FCSTD DOCUMENT  (FreeCAD 0.20R29603 (Git))
Label: assy
License: All rights reserved
LicenseURL: http://en.wikipedia.org/wiki/All_rights_reserved
objects: App::DocumentObjectGroup×3, App::Link×2, PartDesign::CoordinateSystem×1, App::FeaturePython×1, App::Part×1
note: 1 computed .brp shape members not serialized (recipe doc carries the construction recipe); baked Part::Feature solids carry a one-line shape summary decoded from their .brp
EXTERNAL_REF file=spindle.FCStd obj=LCS_1
EXTERNAL_REF file=spindle.FCStd obj=Body
EXTERNAL_REF file=nozzle.FCStd obj=LCS_1
EXTERNAL_REF file=nozzle.FCStd obj=Body

FEATURE [App::DocumentObjectGroup] Parts
FEATURE [PartDesign::CoordinateSystem] LCS_Origin
  AttacherType = Attacher::AttachEngine3D
  MapMode = 2
  Support = -> [X_Axis]
FEATURE [App::DocumentObjectGroup] Constraints
FEATURE [App::FeaturePython] Variables  # WARN: FeaturePython — macro-defined, semantics opaque (R4)
  Type = App::PropertyContainer
FEATURE [App::DocumentObjectGroup] Configurations
FEATURE [App::Link] Body
  AssemblyType = Part::Link
  AttachedBy = #LCS_1
  AttachedTo = Parent Assembly#LCS_Origin
  AttachmentOffset = pos=(0,0,0) rot=(0,-1,0;3.14159rad)
  LinkPlacement = pos=(-5.4e-15,2.06e-14,124) rot=(0,0,-1;1.5708rad)
  LinkedObject = -> <external spindle.FCStd>#Body
  Placement = pos=(-5.4e-15,2.06e-14,124) rot=(0,0,-1;1.5708rad)
  SolverId = Asm4EE
  expr: Placement = LCS_Origin.Placement * AttachmentOffset * spindle#LCS_1.Placement ^ -1
FEATURE [App::Link] Body001
  AssemblyType = Part::Link
  AttachedBy = #LCS_1
  AttachedTo = Body#LCS_1
  LinkPlacement = pos=(-1e-16,5.2e-15,42) rot=(0,0,-1;1.5708rad)
  LinkedObject = -> <external nozzle.FCStd>#Body
  Placement = pos=(-1e-16,5.2e-15,42) rot=(0,0,-1;1.5708rad)
  SolverId = Asm4EE
  expr: Placement = Body.Placement * spindle#LCS_1.Placement * AttachmentOffset * nozzle#LCS_1.Placement ^ -1
FEATURE [App::Part] Model
  AssemblyType = Part::Link
  Group = -> [LCS_Origin,Constraints,Variables,Configurations,Body,Body001]
  Origin = -> Origin
  Type = Assembly

RESOLVED EXTERNAL PARTS (link-assembly join: the EXTERNAL_REF files above that resolve inside this repo's crawl, each included once):
---- part nozzle.FCStd = doc fcstd_8f981881b05c ----
FCSTD DOCUMENT  (FreeCAD 0.20R29603 (Git))
Label: nozzle
License: All rights reserved
LicenseURL: http://en.wikipedia.org/wiki/All_rights_reserved
objects: Sketcher::SketchObject×12, PartDesign::Pocket×4, PartDesign::Pad×3, PartDesign::Plane×2, PartDesign::SubtractiveLoft×1, PartDesign::CoordinateSystem×1, PartDesign::Point×1, PartDesign::AdditivePipe×1, PartDesign::Body×1
note: 35 computed .brp shape members not serialized (recipe doc carries the construction recipe); baked Part::Feature solids carry a one-line shape summary decoded from their .brp

FEATURE [Sketcher::SketchObject] Sketch
  FullyConstrained = true
  MapMode = 5
  Support = -> [XY_Plane]
  sketch-geometry (2):
    g0: Circle CenterX=0 CenterY=0 CenterZ=0 NormalX=0 NormalY=0 NormalZ=1 AngleXU=0 Radius=40.25
    g1: Circle CenterX=0 CenterY=0 CenterZ=0 NormalX=0 NormalY=0 NormalZ=1 AngleXU=0 Radius=45.25
  constraints (4):
    c: Coincident(g0,g-1)
    c: Coincident(g1,g0)
    c: Diameter(g0) = 80.5
    c: Diameter(g1) = 90.5
FEATURE [PartDesign::Pad] Pad
  Direction = (0,0,1)
  Length = 42
  Length2 = 10
  Profile = -> Sketch
  ReferenceAxis = -> Sketch [N_Axis]
  Reversed = true
  Type = 0
FEATURE [Sketcher::SketchObject] Sketch001
  FullyConstrained = true
  MapMode = 5
  Placement = pos=(0,0,-42) rot=(1,0,0;3.14159rad)
  Support = -> [Pad]
  sketch-geometry (1):
    g0: Circle CenterX=0 CenterY=0 CenterZ=0 NormalX=0 NormalY=0 NormalZ=1 AngleXU=0 Radius=45.25
  constraints (2):
    c: Coincident(g0,g-1)
    c: Diameter(g0) = 90.5
FEATURE [PartDesign::Pad] Pad001
  BaseFeature = -> Pad
  Direction = (0,0,-1)
  Length = 5
  Length2 = 10
  Profile = -> Sketch001
  ReferenceAxis = -> Sketch001 [N_Axis]
  Type = 0
FEATURE [Sketcher::SketchObject] Sketch002
  FullyConstrained = true
  MapMode = 5
  Placement = pos=(0,0,-47) rot=(1,0,0;3.14159rad)
  Support = -> [Pad001]
  sketch-geometry (1):
    g0: Circle CenterX=0 CenterY=0 CenterZ=0 NormalX=0 NormalY=0 NormalZ=1 AngleXU=0 Radius=36.5
  constraints (2):
    c: Coincident(g0,g-1)
    c: Diameter(g0) = 73
FEATURE [PartDesign::Pocket] Pocket
  BaseFeature = -> Pad001
  Direction = (0,0,1)
  Length = 5
  Length2 = 5
  Profile = -> Sketch002
  ReferenceAxis = -> Sketch002 [N_Axis]
  Type = 0
FEATURE [Sketcher::SketchObject] Sketch003
  FullyConstrained = true
  MapMode = 5
  Placement = pos=(0,0,0) rot=(0.57735,0.57735,0.57735;2.0944rad)
  Support = -> [YZ_Plane]
  sketch-geometry (4):
    g0: LineSegment StartX=-2 StartY=0 StartZ=0 EndX=2 EndY=0 EndZ=0
    g1: LineSegment StartX=2 StartY=0 StartZ=0 EndX=2 EndY=-35 EndZ=0
    g2: LineSegment StartX=2 StartY=-35 StartZ=0 EndX=-2 EndY=-35 EndZ=0
    g3: LineSegment StartX=-2 StartY=-35 StartZ=0 EndX=-2 EndY=0 EndZ=0
  constraints (11):
    c: Coincident(g0,g1)
    c: Coincident(g1,g2)
    c: Coincident(g2,g3)
    c: Coincident(g3,g0)
    c: Horizontal(g0)
    c: Vertical(g1)
    c: Vertical(g3)
    c: PointOnObject(g0,g-1)
    c: Symmetric(g2,g1,g-2)
    c: DistanceX(g2,g2) = 4
    c: DistanceY(g1,g1) = 35
FEATURE [PartDesign::Pocket] Pocket001
  BaseFeature = -> Pocket
  Direction = (-1,2e-16,-3e-16)
  Length = 90.5
  Length2 = 5
  Midplane = true
  Profile = -> Sketch003
  ReferenceAxis = -> Sketch003 [N_Axis]
  Type = 0
FEATURE [Sketcher::SketchObject] Sketch004
  FullyConstrained = true
  MapMode = 5
  Placement = pos=(0,0,0) rot=(1,0,0;1.5708rad)
  Support = -> [XZ_Plane]
  sketch-geometry (4):
    g0: LineSegment StartX=-2 StartY=0 StartZ=0 EndX=2 EndY=0 EndZ=0
    g1: LineSegment StartX=2 StartY=0 StartZ=0 EndX=2 EndY=-35 EndZ=0
    g2: LineSegment StartX=2 StartY=-35 StartZ=0 EndX=-2 EndY=-35 EndZ=0
    g3: LineSegment StartX=-2 StartY=-35 StartZ=0 EndX=-2 EndY=0 EndZ=0
  constraints (11):
    c: Coincident(g0,g1)
    c: Coincident(g1,g2)
    c: Coincident(g2,g3)
    c: Coincident(g3,g0)
    c: Horizontal(g0)
    c: Vertical(g1)
    c: Vertical(g3)
    c: PointOnObject(g0,g-1)
    c: DistanceX(g2,g2) = 4
    c: Symmetric(g1,g2,g-2)
    c: DistanceY(g1,g1) = 35
FEATURE [PartDesign::Pocket] Pocket002
  BaseFeature = -> Pocket001
  Direction = (0,1,-2e-16)
  Length = 90.5
  Length2 = 5
  Midplane = true
  Profile = -> Sketch004
  ReferenceAxis = -> Sketch004 [N_Axis]
  Type = 0
FEATURE [Sketcher::SketchObject] Sketch005
  ExternalGeometry = -> [Pocket002]
  FullyConstrained = true
  MapMode = 5
  Support = -> [Pocket002]
  sketch-geometry (5):
    g0: LineSegment StartX=39.5904 StartY=-21.9127 StartZ=0 EndX=51.6112 EndY=-33.9335 EndZ=0
    g1: LineSegment StartX=21.9127 StartY=-39.5904 StartZ=0 EndX=33.9335 EndY=-51.6112 EndZ=0
    g2: LineSegment StartX=0 StartY=0 StartZ=0 EndX=141.421 EndY=-141.421 EndZ=0
    g3: ArcOfCircle CenterX=53.812 CenterY=-53.812 CenterZ=0 NormalX=0 NormalY=0 NormalZ=1 AngleXU=0 Radius=20 StartAngle=3.03133 EndAngle=7.96425
    g4: ArcOfCircle CenterX=53.812 CenterY=-53.812 CenterZ=0 NormalX=0 NormalY=0 NormalZ=1 AngleXU=0 Radius=34.926 StartAngle=1.99018 EndAngle=2.72221
  constraints (15):
    c: PointOnObject(g0,g-3)
    c: Angle(g-1,g0) = 2.35619
    c: Parallel(g1,g0)
    c: Equal(g1,g0)
    c: Coincident(g2,g-3)
    c: Distance(g2) = 200
    c: Symmetric(g1,g0,g2)
    c: Distance(g1,g0) = 25
    c: Distance(g0) = 17
    c: Coincident(g3,g0)
    c: Coincident(g3,g1)
    c: Coincident(g4,g3)
    c: Coincident(g4,g1)
    c: Coincident(g4,g0)
    c: Diameter(g3) = 40
FEATURE [PartDesign::Pad] Pad002
  BaseFeature = -> Pocket002
  Direction = (0,0,1)
  Length = 47
  Length2 = 10
  Profile = -> Sketch005
  ReferenceAxis = -> Sketch005 [N_Axis]
  Reversed = true
  Type = 0
FEATURE [Sketcher::SketchObject] Sketch006
  ExternalGeometry = -> [Pad002]
  FullyConstrained = true
  MapMode = 5
  Support = -> [Pad002]
  sketch-geometry (1):
    g0: Circle CenterX=53.812 CenterY=-53.812 CenterZ=0 NormalX=0 NormalY=0 NormalZ=1 AngleXU=0 Radius=17.5
  constraints (2):
    c: Coincident(g0,g-3)
    c: Diameter(g0) = 35
FEATURE [Sketcher::SketchObject] Sketch007
  ExternalGeometry = -> [Pad002]
  FullyConstrained = true
  MapMode = 5
  Placement = pos=(0,0,-47) rot=(1,0,0;3.14159rad)
  Support = -> [Pad002]
  sketch-geometry (1):
    g0: Circle CenterX=53.812 CenterY=53.812 CenterZ=0 NormalX=0 NormalY=0 NormalZ=1 AngleXU=0 Radius=17
  constraints (2):
    c: Coincident(g0,g-3)
    c: Diameter(g0) = 34
FEATURE [PartDesign::SubtractiveLoft] SubtractiveLoft
  BaseFeature = -> Pad002
  Closed = false
  Profile = -> Sketch006
  Ruled = false
  Sections = -> [Sketch007]
FEATURE [Sketcher::SketchObject] Sketch008
  ExternalGeometry = -> [SubtractiveLoft]
  FullyConstrained = true
  MapMode = 5
  Support = -> [SubtractiveLoft]
  sketch-geometry (4):
    g0: ArcOfCircle CenterX=0 CenterY=-7.6e-15 CenterZ=0 NormalX=0 NormalY=0 NormalZ=1 AngleXU=0 Radius=45.25 StartAngle=5.2179 EndAngle=5.77767
    g1: ArcOfCircle CenterX=0 CenterY=-7.6e-15 CenterZ=0 NormalX=0 NormalY=0 NormalZ=1 AngleXU=0 Radius=48.1404 StartAngle=5.23512 EndAngle=5.76045
    g2: LineSegment StartX=41.7117 StartY=-24.034 StartZ=0 EndX=39.5904 EndY=-21.9127 EndZ=0
    g3: LineSegment StartX=24.034 StartY=-41.7117 StartZ=0 EndX=21.9127 EndY=-39.5904 EndZ=0
  constraints (11):
    c: PointOnObject(g0,g-2)
    c: Coincident(g0,g-3)
    c: Coincident(g0,g-3)
    c: Coincident(g1,g0)
    c: PointOnObject(g1,g-5)
    c: PointOnObject(g1,g-4)
    c: Coincident(g2,g1)
    c: Coincident(g2,g0)
    c: Coincident(g3,g1)
    c: Coincident(g3,g0)
    c: Distance(g2) = 3
FEATURE [PartDesign::Pocket] Pocket003
  BaseFeature = -> SubtractiveLoft
  Direction = (0,0,-1)
  Length = 15
  Length2 = 5
  Profile = -> Sketch008
  ReferenceAxis = -> Sketch008 [N_Axis]
  Type = 0
FEATURE [PartDesign::CoordinateSystem] LCS_1
  AttacherType = Attacher::AttachEngine3D
  MapMode = 11
  Placement = pos=(0,0,-42) rot=(0.707107,-0.707107,0;3.14159rad)
  Support = -> [Pocket003]
FEATURE [Sketcher::SketchObject] Sketch009
  ExternalGeometry = -> [Pocket003]
  FullyConstrained = true
  MapMode = 5
  Placement = pos=(0,0,-47) rot=(1,0,0;3.14159rad)
  Support = -> [Pocket003]
  sketch-geometry (2):
    g0: Circle CenterX=53.812 CenterY=53.812 CenterZ=0 NormalX=0 NormalY=0 NormalZ=1 AngleXU=0 Radius=17
    g1: Circle CenterX=53.812 CenterY=53.812 CenterZ=0 NormalX=0 NormalY=0 NormalZ=1 AngleXU=0 Radius=20
  constraints (4):
    c: Coincident(g0,g-3)
    c: Diameter(g0) = 34
    c: Coincident(g1,g0)
    c: Diameter(g1) = 40
FEATURE [PartDesign::Plane] DatumPlane
  AttachmentOffset = pos=(0,0,0) rot=(-0.357407,0.862856,0.357407;1.71777rad)
  Length = 152.689
  MapMode = 11
  Placement = pos=(53.812,-53.812,-47) rot=(0.357407,-0.862856,0.357407;1.71777rad)
  ResizeMode = 0
  Support = -> [Pocket003]
  Width = 197.255
FEATURE [Sketcher::SketchObject] Sketch010
  FullyConstrained = true
  MapMode = 5
  Placement = pos=(53.812,-53.812,-47) rot=(0.357407,-0.862856,0.357407;1.71777rad)
  Support = -> [DatumPlane]
  sketch-geometry (6):
    g0: Circle CenterX=0 CenterY=0 CenterZ=0 NormalX=0 NormalY=0 NormalZ=1 AngleXU=0 Radius=1
    g1: Circle CenterX=-35 CenterY=-3 CenterZ=0 NormalX=0 NormalY=0 NormalZ=1 AngleXU=0 Radius=1
    g2: Circle CenterX=-50 CenterY=40 CenterZ=0 NormalX=0 NormalY=0 NormalZ=1 AngleXU=0 Radius=1
    g3: BSplineCurve PolesCount=3 KnotsCount=2 Degree=2 IsPeriodic=0
    g4: GeomPoint X=0 Y=0 Z=0
    g5: GeomPoint X=-50 Y=40 Z=0
  constraints (13):
    c: Weight(g0) = 1
    c: Coincident(g3,g-1)
    c: Equal(g0,g1)
    c: Equal(g0,g2)
    c: InternalAlignment(g0,g3)
    c: InternalAlignment(g1,g3)
    c: InternalAlignment(g2,g3)
    c: InternalAlignment(g4,g3)
    c: InternalAlignment(g5,g3)
    c: DistanceX(g3,g3) = 50
    c: DistanceY(g3,g3) = 40
    c: DistanceY(g1,g3) = 3
    c: DistanceX(g1,g3) = 35
FEATURE [PartDesign::Point] DatumPoint
  AttacherType = Attacher::AttachEnginePoint
  MapMode = 37
  Placement = pos=(25.5278,-25.5278,-97) rot=(0,0,1;0rad)
  Support = -> [Sketch010]
FEATURE [PartDesign::Plane] DatumPlane002
  AttachmentOffset = pos=(0,0,0) rot=(0.300549,0.124491,0.945607;0.825727rad)
  Length = 204.589
  MapMode = 2
  Placement = pos=(25.5278,-25.5278,-97) rot=(0.300549,0.124491,0.945607;0.825727rad)
  ResizeMode = 0
  Support = -> [DatumPoint]
  Width = 230.897
FEATURE [Sketcher::SketchObject] Sketch012
  FullyConstrained = true
  MapMode = 5
  Placement = pos=(25.5278,-25.5278,-97) rot=(0.300549,0.124491,0.945607;0.825727rad)
  Support = -> [DatumPlane002]
  sketch-geometry (8):
    g0: ArcOfCircle CenterX=-17.5 CenterY=0 CenterZ=0 NormalX=0 NormalY=0 NormalZ=1 AngleXU=0 Radius=5 StartAngle=1.5708 EndAngle=4.71239
    g1: ArcOfCircle CenterX=17.5 CenterY=0 CenterZ=0 NormalX=0 NormalY=0 NormalZ=1 AngleXU=0 Radius=5 StartAngle=4.71239 EndAngle=7.85398
    g2: LineSegment StartX=-17.5 StartY=-5 StartZ=0 EndX=17.5 EndY=-5 EndZ=0
    g3: LineSegment StartX=17.5 StartY=5 StartZ=0 EndX=-17.5 EndY=5 EndZ=0
    g4: ArcOfCircle CenterX=-17.5 CenterY=0 CenterZ=0 NormalX=0 NormalY=0 NormalZ=1 AngleXU=0 Radius=7 StartAngle=1.5708 EndAngle=4.71239
    g5: ArcOfCircle CenterX=17.5 CenterY=0 CenterZ=0 NormalX=0 NormalY=0 NormalZ=1 AngleXU=0 Radius=7 StartAngle=4.71239 EndAngle=7.85398
    g6: LineSegment StartX=-17.5 StartY=-7 StartZ=0 EndX=17.5 EndY=-7 EndZ=0
    g7: LineSegment StartX=17.5 StartY=7 StartZ=0 EndX=-17.5 EndY=7 EndZ=0
  constraints (17):
    c: Tangent(g0,g2) = -1.5708
    c: Tangent(g2,g1) = -1.5708
    c: Tangent(g1,g3) = -1.5708
    c: Tangent(g3,g0) = -1.5708
    c: Equal(g0,g1)
    c: PointOnObject(g0,g-1)
    c: Tangent(g4,g6) = -1.5708
    c: Tangent(g6,g5) = -1.5708
    c: Tangent(g5,g7) = -1.5708
    c: Tangent(g7,g4) = -1.5708
    c: Equal(g4,g5)
    c: DistanceX(g0,g1) = 35
    c: DistanceY(g1,g1) = 10
    c: Symmetric(g1,g0,g-1)
    c: Symmetric(g5,g4,g-1)
    c: DistanceY(g5,g5) = 14
    c: Coincident(g5,g1)
FEATURE [PartDesign::AdditivePipe] AdditivePipe
  AuxilleryCurvelinear = true
  AuxillerySpineTangent = false
  BaseFeature = -> Pocket003
  Binormal = (0,0,0)
  Mode = 0
  Profile = -> Sketch009
  Sections = -> [Sketch012]
  Spine = -> Sketch010
  SpineTangent = false
  Transformation = 1
  Transition = 0
FEATURE [PartDesign::Body] Body
  Group = -> [Sketch,Pad,Sketch001,Pad001,Sketch002,Pocket,Sketch003,Pocket001,Sketch004,Pocket002,Sketch005,Pad002,Sketch006,Sketch007,SubtractiveLoft,Sketch008,Pocket003,LCS_1,Sketch009,DatumPlane,Sketch010,DatumPoint,DatumPlane002,Sketch012,AdditivePipe]
  Origin = -> Origin
  Tip = -> AdditivePipe
---- part spindle.FCStd = doc fcstd_ea920163136a ----
FCSTD DOCUMENT  (FreeCAD 0.20R29603 (Git))
Label: spindle
License: All rights reserved
LicenseURL: http://en.wikipedia.org/wiki/All_rights_reserved
objects: Sketcher::SketchObject×5, PartDesign::Pad×5, PartDesign::CoordinateSystem×1, PartDesign::Body×1
note: 17 computed .brp shape members not serialized (recipe doc carries the construction recipe); baked Part::Feature solids carry a one-line shape summary decoded from their .brp

FEATURE [Sketcher::SketchObject] Sketch
  FullyConstrained = true
  MapMode = 5
  Support = -> [XY_Plane]
  sketch-geometry (1):
    g0: Circle CenterX=0 CenterY=0 CenterZ=0 NormalX=0 NormalY=0 NormalZ=1 AngleXU=0 Radius=40
  constraints (2):
    c: Coincident(g0,g-1)
    c: Diameter(g0) = 80
FEATURE [PartDesign::Pad] Pad
  Direction = (0,0,1)
  Length = 100
  Length2 = 10
  Profile = -> Sketch
  ReferenceAxis = -> Sketch [N_Axis]
  Reversed = true
  Type = 0
FEATURE [Sketcher::SketchObject] Sketch001
  FullyConstrained = true
  MapMode = 5
  Placement = pos=(0,0,-100) rot=(1,0,0;3.14159rad)
  Support = -> [Pad]
  sketch-geometry (1):
    g0: Circle CenterX=0 CenterY=0 CenterZ=0 NormalX=0 NormalY=0 NormalZ=1 AngleXU=0 Radius=39.5
  constraints (2):
    c: Coincident(g0,g-1)
    c: Diameter(g0) = 79
FEATURE [PartDesign::Pad] Pad001
  BaseFeature = -> Pad
  Direction = (0,0,-1)
  Length = 12
  Length2 = 10
  Profile = -> Sketch001
  ReferenceAxis = -> Sketch001 [N_Axis]
  Type = 0
FEATURE [Sketcher::SketchObject] Sketch002
  FullyConstrained = true
  MapMode = 5
  Placement = pos=(0,0,-112) rot=(1,0,0;3.14159rad)
  Support = -> [Pad001]
  sketch-geometry (1):
    g0: Circle CenterX=0 CenterY=0 CenterZ=0 NormalX=0 NormalY=0 NormalZ=1 AngleXU=0 Radius=35.75
  constraints (2):
    c: Coincident(g0,g-1)
    c: Diameter(g0) = 71.5
FEATURE [PartDesign::Pad] Pad002
  BaseFeature = -> Pad001
  Direction = (0,0,-1)
  Length = 12
  Length2 = 10
  Profile = -> Sketch002
  ReferenceAxis = -> Sketch002 [N_Axis]
  Type = 0
FEATURE [Sketcher::SketchObject] Sketch003
  FullyConstrained = true
  MapMode = 5
  Placement = pos=(0,0,-124) rot=(1,0,0;3.14159rad)
  Support = -> [Pad002]
  sketch-geometry (1):
    g0: Circle CenterX=0 CenterY=0 CenterZ=0 NormalX=0 NormalY=0 NormalZ=1 AngleXU=0 Radius=17
  constraints (2):
    c: Coincident(g0,g-1)
    c: Diameter(g0) = 34
FEATURE [PartDesign::Pad] Pad003
  BaseFeature = -> Pad002
  Direction = (0,0,-1)
  Length = 56
  Length2 = 10
  Profile = -> Sketch003
  ReferenceAxis = -> Sketch003 [N_Axis]
  Type = 0
FEATURE [PartDesign::CoordinateSystem] LCS_1
  AttacherType = Attacher::AttachEngine3D
  MapMode = 11
  Placement = pos=(0,0,-124) rot=(0.707107,-0.707107,0;3.14159rad)
  Support = -> [Pad003]
FEATURE [Sketcher::SketchObject] Sketch004
  FullyConstrained = true
  MapMode = 5
  Placement = pos=(0,0,-180) rot=(1,0,0;3.14159rad)
  Support = -> [Pad003]
  sketch-geometry (1):
    g0: Circle CenterX=0 CenterY=0 CenterZ=0 NormalX=0 NormalY=0 NormalZ=1 AngleXU=0 Radius=3
  constraints (2):
    c: Coincident(g0,g-1)
    c: Diameter(g0) = 6
FEATURE [PartDesign::Pad] Pad004
  BaseFeature = -> Pad003
  Direction = (0,0,-1)
  Length = 22
  Length2 = 10
  Profile = -> Sketch004
  ReferenceAxis = -> Sketch004 [N_Axis]
  Type = 0
FEATURE [PartDesign::Body] Body
  Group = -> [Sketch,Pad,Sketch001,Pad001,Sketch002,Pad002,Sketch003,Pad003,LCS_1,Sketch004,Pad004]
  Origin = -> Origin
  Tip = -> Pad004
